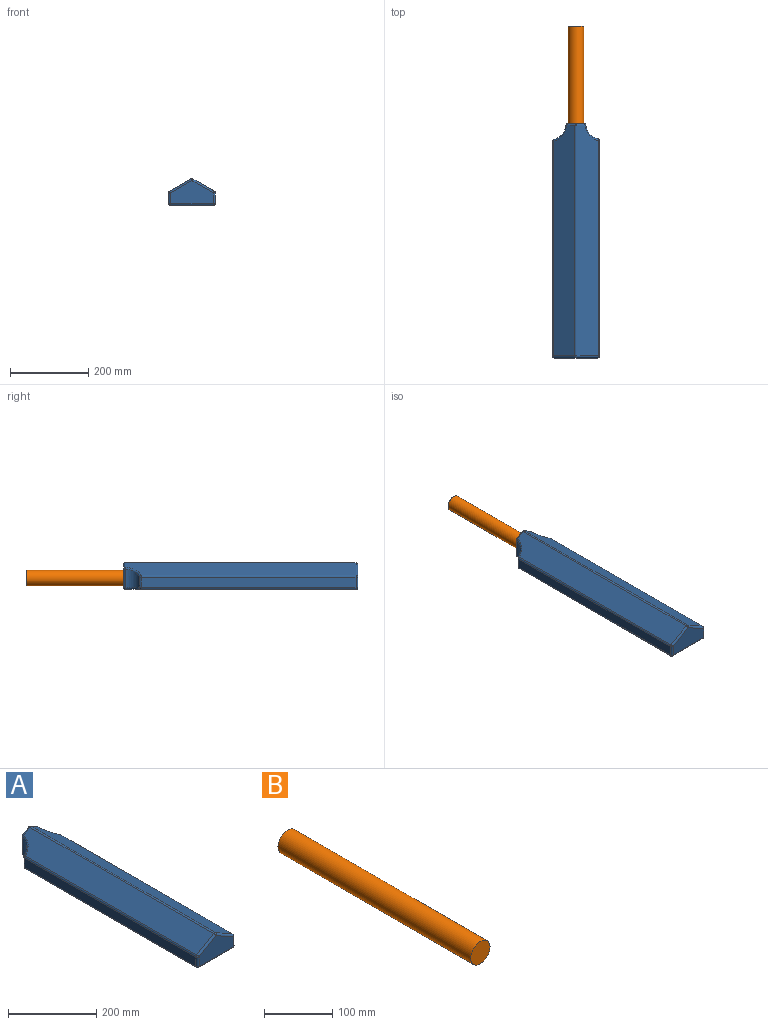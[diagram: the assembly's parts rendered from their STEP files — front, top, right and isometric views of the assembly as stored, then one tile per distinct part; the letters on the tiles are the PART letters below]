
ASSEMBLY  parts=2 mates=1
PART A: 46 faces, bbox 122.9x600x2000.9 mm
  f0: plane 58.34x40.96mm, normal (0,1,0), area 890.4mm2, adj f2,f5,f7,f26,f31,f40
  f1: plane 589.84x109.84mm, normal (0,0,-1), area 62832.1mm2, adj f6,f7,f8,f23,f32,f39
  f2: cylinder r=5.08mm len=23mm, axis (-0.86,0,-0.5), area 188.7mm2, adj f0,f12,f18,f33
  f3: cylinder r=5.08mm len=549.07mm, axis (0,1,0), area 2920.9mm2, adj f12,f13,f16,f37
  f4: cylinder r=5.08mm len=551.03mm, axis (0,1,0), area 2931.4mm2, adj f10,f11,f22,f45
  f5: cylinder r=5.08mm len=23.04mm, axis (-0.87,0,0.5), area 188.7mm2, adj f0,f11,f18,f42
  f6: cylinder r=5.08mm len=549.09mm, axis (0,-1,0), area 4374.1mm2, adj f1,f13,f21,f34
  f7: cylinder r=5.08mm len=40.96mm, axis (1,0,0), area 326.8mm2, adj f0,f1,f30,f38
  f8: cylinder r=5.08mm len=551.02mm, axis (0,1,0), area 4404.4mm2, adj f1,f10,f25,f41
  f9: plane 109.91x58.34mm, normal (0,-1,0), area 4666.2mm2, adj f14,f19,f20,f23,f24
  f10: plane 551.03x26.78mm, normal (1,0,0), area 14754.1mm2, adj f4,f8,f24,f43
  f11: plane 589.84x55.01mm, normal (0.5,0,0.87), area 36298.9mm2, adj f4,f5,f15,f20,f44
  f12: plane 589.84x54.83mm, normal (-0.5,0,0.86), area 36253mm2, adj f2,f3,f14,f15,f35
  f13: plane 549.1x26.48mm, normal (-1,0,0), area 14540mm2, adj f3,f6,f19,f36
  f14: cylinder r=5.08mm len=57.39mm, axis (0.86,0,0.5), area 506mm2, adj f9,f12,f16,f17
  f15: cylinder r=5.08mm len=589.84mm, axis (0,1,0), area 3137.8mm2, adj f11,f12,f17,f18
  f16: sphere r=5.08mm, area 27mm2, adj f3,f14,f19
  f17: sphere r=5.08mm, area 27mm2, adj f14,f15,f20
  f18: sphere r=5.08mm, area 27mm2, adj f2,f5,f15
  f19: cylinder r=5.08mm len=26.49mm, axis (0,0,1), area 211.3mm2, adj f9,f13,f16,f21
  f20: cylinder r=5.08mm len=57.53mm, axis (0.87,0,-0.5), area 506mm2, adj f9,f11,f17,f22
  f21: sphere r=5.08mm, area 40.5mm2, adj f6,f19,f23
  f22: sphere r=5.08mm, area 27mm2, adj f4,f20,f24
  f23: cylinder r=5.08mm len=109.84mm, axis (-1,0,0), area 876.5mm2, adj f1,f9,f21,f25
  f24: cylinder r=5.08mm len=26.79mm, axis (0,0,-1), area 213.7mm2, adj f9,f10,f22,f25
  f25: sphere r=5.08mm, area 40.6mm2, adj f8,f23,f24
  f26: cylinder r=20mm len=150mm, axis (0,1,0), area 18849.6mm2, adj f0,f27
  f27: plane 40x40mm, normal (0,1,0), area 1256.6mm2, adj f26
  f28: cylinder r=40mm len=46.57mm, axis (0,0,-1), area 1916.1mm2, adj f39,f40,f43,f44
  f29: cylinder r=42.57mm len=46.46mm, axis (0,0,-1), area 1964.8mm2, adj f31,f32,f35,f36
  f30: sphere r=5.08mm, area 38.4mm2, adj f7,f31,f32
  f31: cylinder r=5.08mm len=46.46mm, axis (0,0,-1), area 345.5mm2, adj f0,f29,f30,f33
  f32: torus R=47.65mm, axis (0,0,1), area 420.5mm2, adj f1,f29,f30,f34
  f33: sphere r=5.08mm, area 25.4mm2, adj f2,f31,f35
  f34: sphere r=5.08mm, area 34.9mm2, adj f6,f32,f36
  f35: bspline ~41.31x34.58mm, area 350.5mm2, adj f12,f29,f33,f37
  f36: bspline ~29.07x4.91mm, area 174.1mm2, adj f13,f29,f34,f37
  f37: sphere r=5.08mm, area 21.2mm2, adj f3,f35,f36
  f38: sphere r=5.08mm, area 37.6mm2, adj f7,f39,f40
  f39: torus R=45.08mm, axis (0,0,1), area 410.4mm2, adj f1,f28,f38,f41
  f40: cylinder r=5.08mm len=46.57mm, axis (0,0,-1), area 344.9mm2, adj f0,f28,f38,f42
  f41: sphere r=5.08mm, area 36mm2, adj f8,f39,f43
  f42: sphere r=5.08mm, area 25.4mm2, adj f5,f40,f44
  f43: bspline ~2000.9x9.02mm, area 182.4mm2, adj f10,f28,f41,f45
  f44: bspline ~39.38x34.64mm, area 345.9mm2, adj f11,f28,f42,f45
  f45: sphere r=5.08mm, area 22.4mm2, adj f4,f43,f44
PART B: 3 faces, bbox 40x400x40 mm
  f0: cylinder r=20mm len=400mm, axis (0,1,0), area 50265.5mm2, adj f1,f2
  f1: plane 40x40mm, normal (0,-1,0), area 1256.6mm2, adj f0
  f2: plane 40x40mm, normal (0,1,0), area 1256.6mm2, adj f0
PLACE A t=(-272.53,65.33,-150.2)mm
PLACE B t=(-272.53,315.33,-121)mm
MATE fastened B.f0 <-> A.f26  axis (0,-1,0) through (-272.53,-84.67,-121)mm
